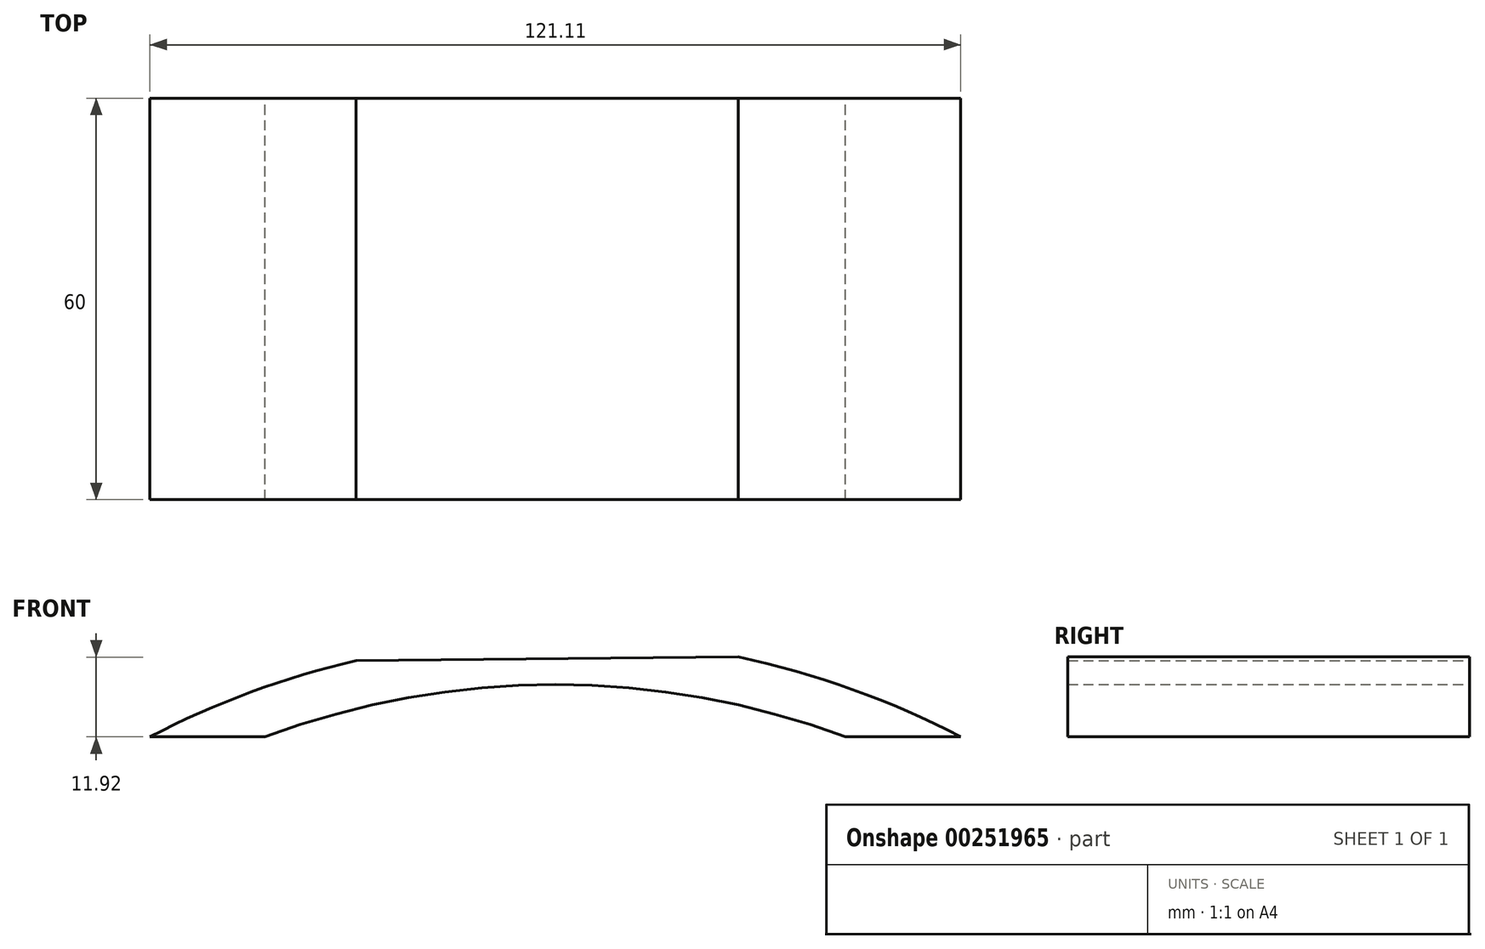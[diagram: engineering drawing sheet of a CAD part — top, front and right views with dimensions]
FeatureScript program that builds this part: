
annotation { "Feature Type Name" : "Feature", "Feature Type Description" : "" }
export const myFeature = defineFeature(function(context is Context, id is Id, definition is map)
    precondition{}
    {
        {
            var Q0;
            Q0=qCreatedBy(makeId("Front.planeOp"),FACE);
            var sketch = newSketch(context, id + "F0", { "sketchPlane" : qUnion([Q0])});
            skArc(sketch, "E0", {"start": v(71.67, 0) * mm, "mid": v(-15.83, 33.42) * mm, "end": v(-103.33, 0) * mm});
            skLineSegment(sketch, "E1", {"start": v(-103.33, 0) * mm, "end": v(-92.43, 0) * mm});
            skArc(sketch, "E2.0", {"start": v(60.77, 0) * mm, "mid": v(-15.83, 26.42) * mm, "end": v(-92.43, 0) * mm});
            skLineSegment(sketch, "E3.trimOffspring", {"start": v(60.77, 0) * mm, "end": v(71.67, 0) * mm});
            skLineSegment(sketch, "E4", {"start": v(-45.6, 30) * mm, "end": v(11.5, 30.54) * mm});
            skLineSegment(sketch, "E5", {"start": v(27.52, 18.62) * mm, "end": v(44.73, 18.62) * mm});
            skLineSegment(sketch, "E6", {"start": v(-59.17, 18.62) * mm, "end": v(-76.38, 18.62) * mm});
            skSolve(sketch);
        }
        {
            var Q0;
            Q0=makeQuery(id+"F0.imprint","IMPRINT",FACE,{"disambiguationData":[TD([[makeQuery(id+"F0.imprint","IMPRINT",EDGE,{"derivedFrom":sQuery(id+"F0.wireOp",EDGE,"E0")}),1.0]])]});
            extrude(context, id + "F1", {"entities" : qUnion([Q0]), "depth" : 60 * mm});
        }
    });
